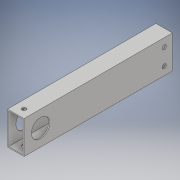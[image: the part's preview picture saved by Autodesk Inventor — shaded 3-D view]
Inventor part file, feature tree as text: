
AUTODESK INVENTOR PART (.ipt)
format: ipt  version: 2018 (Build 220112000, 112)  size: 118,784 bytes
history: native  units: in
note: dims shown in document units (in); Inventor stores cm internally (conversion verified against a paired STEP export)
features: hole x4, extrude x1, shell x1, sketch x1
ambient origin geometry x8: Origin, YZ Plane, XZ Plane, XY Plane, X Axis, Y Axis, Z Axis, Center Point
bodies: Solid1 (feature_tree)
feature tree (7):
  extrude  "Extrusion1"  Depth=2.0in
  shell  "Shell1"  Thickness=9.0in
  hole  "Hole3"  [1 undecoded]
  hole  "Hole4"  [1 undecoded]
  hole  "Hole5"  [1 undecoded]
  hole  "Hole6"  [1 undecoded]
  sketch  "Sketch1"  dims[d0=1.0in d1=2.0in d2=9.0in d3=0.0in d4=0.0625in d23=0.5in d24=0.5in d25=0.25in d26=0.75in d27=0.375in d28=0.25in d29=0.5635in d30=1.0in d31=0.8108in d32=0.5in d33=0.5in d34=0.25in d35=0.75in d36=0.375in d37=0.25in d38=0.5635in d39=1.0in d40=0.8108in d41=1.0in d42=1.0in d43=1.125in d44=0.75in d45=0.375in d46=0.25in d47=0.5635in d48=1.0in d49=0.8108in d50=0.5in d51=0.5in d52=0.25in d53=0.75in d54=0.375in d55=0.25in d56=0.5635in d57=1.0in d58=0.8108in]
note: 4 required parameter values undecoded (feature->parameter linkage not recoverable at this tier; creation-order binding heuristic only, values carry confidence <= 0.55)
